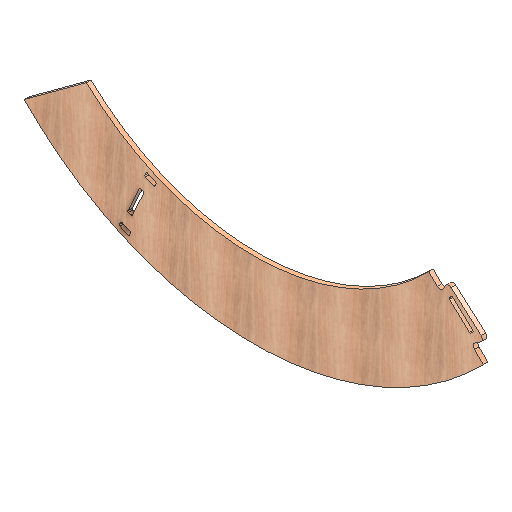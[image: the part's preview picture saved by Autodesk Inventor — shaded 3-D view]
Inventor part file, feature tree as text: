
AUTODESK INVENTOR PART (.ipt)
format: ipt  version: 2021 (Build 250183000, 183)  size: 275,456 bytes
history: native  units: mm
features: other x2, extrude x2, hole x1
ambient origin geometry x8: Origin, YZ Plane, XZ Plane, XY Plane, X Axis, Y Axis, Z Axis, Center Point
bodies: Body1 (feature_tree)
feature tree (5):
  other  "CONTOURS"
  hole  "HOLES"  [1 undecoded]
  other  "LETTERS"
  extrude  "Extrusion2"  Depth=971.444169mm
  extrude  "Extrusion3"  Depth=18.0mm TaperAngle=0.0deg
note: 1 required parameter value undecoded (feature->parameter linkage not recoverable at this tier; creation-order binding heuristic only, values carry confidence <= 0.55)
